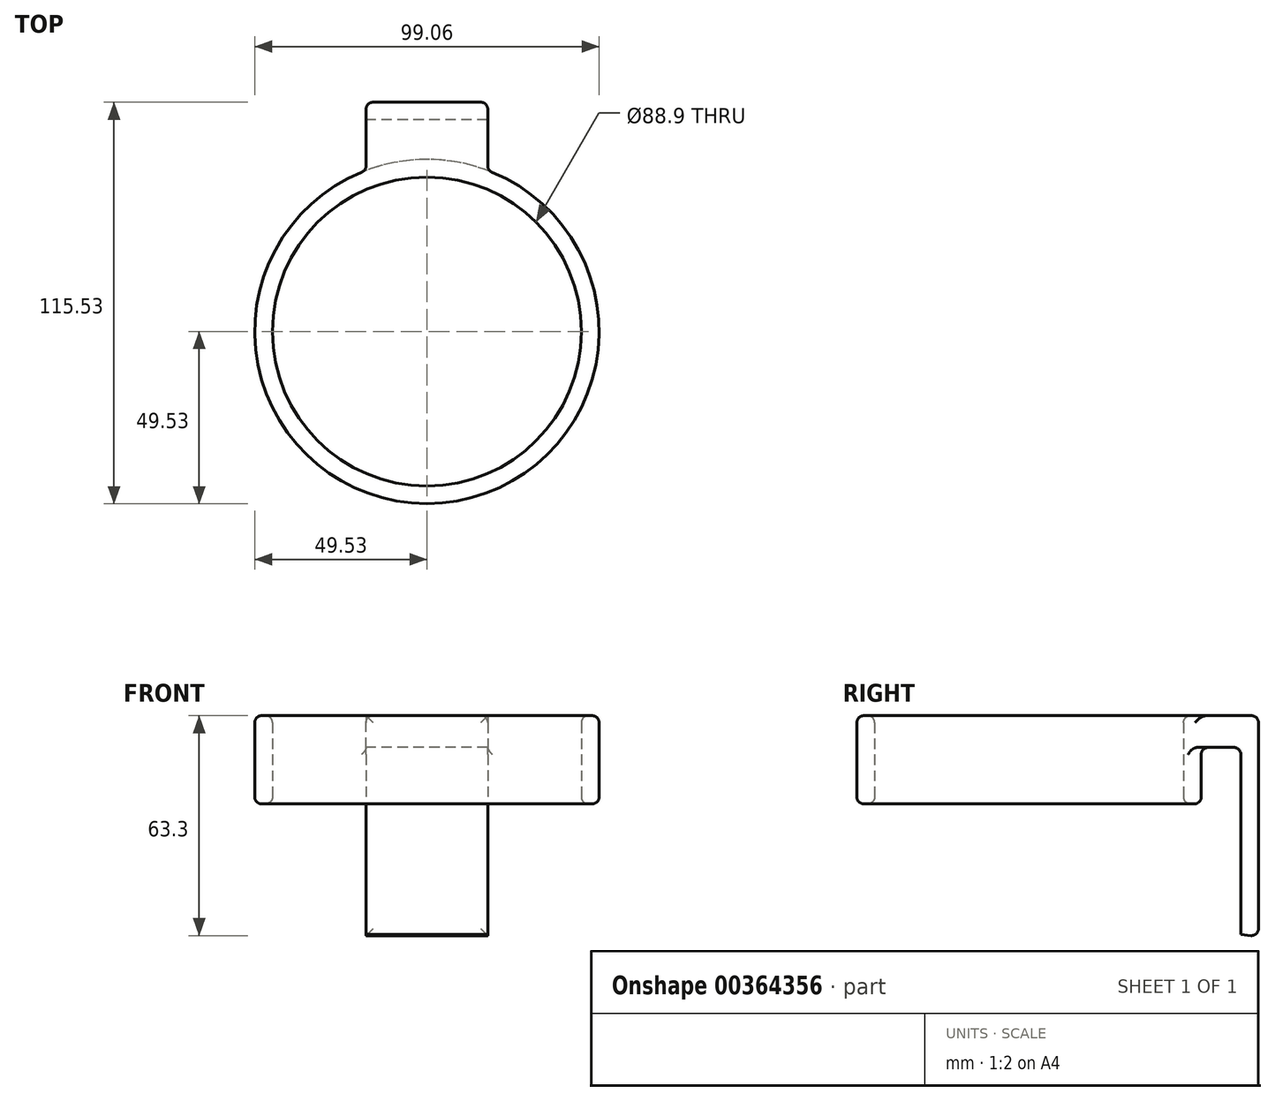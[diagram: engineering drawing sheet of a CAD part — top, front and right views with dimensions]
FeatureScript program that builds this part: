
annotation { "Feature Type Name" : "Feature", "Feature Type Description" : "" }
export const myFeature = defineFeature(function(context is Context, id is Id, definition is map)
    precondition{}
    {
        {
            var Q0;
            Q0=qCreatedBy(makeId("Top.planeOp"),FACE);
            var sketch = newSketch(context, id + "F0", { "sketchPlane" : qUnion([Q0])});
            skCircle(sketch, "E0", {"center": v(0, 0) * mm, "radius": 44.45 * mm});
            skCircle(sketch, "E1", {"center": v(0, 0) * mm, "radius": 49.53 * mm});
            skSolve(sketch);
        }
        {
            var Q0;
            Q0 = qSketchRegion(id + "F0", true);
            extrude(context, id + "F1", {"entities" : qUnion([Q0]), "depth" : 25.4 * mm});
        }
        {
            var Q0;
            Q0=qCreatedBy(makeId("Right.planeOp"),FACE);
            var sketch = newSketch(context, id + "F2", { "sketchPlane" : qUnion([Q0])});
            skLineSegment(sketch, "E2", {"start": v(45.68, 25.4) * mm, "end": v(66, 25.4) * mm});
            skLineSegment(sketch, "E3", {"start": v(66, 25.4) * mm, "end": v(66, 25.4) * mm});
            skLineSegment(sketch, "E4", {"start": v(66, -38.1) * mm, "end": v(66, 25.4) * mm});
            skLineSegment(sketch, "E5", {"start": v(45.68, 25.4) * mm, "end": v(45.68, 16.24) * mm});
            skLineSegment(sketch, "E6", {"start": v(45.68, 16.24) * mm, "end": v(45.68, 16.24) * mm});
            skLineSegment(sketch, "E7", {"start": v(45.68, 16.24) * mm, "end": v(60.96, 16.24) * mm});
            skLineSegment(sketch, "E8", {"start": v(60.96, 16.24) * mm, "end": v(60.96, -37.61) * mm});
            skLineSegment(sketch, "E9", {"start": v(60.96, -37.61) * mm, "end": v(66, -38.1) * mm});
            skPoint(sketch, "E10.start.orphan", {"position": v(60.96, 17.2) * mm});
            skSolve(sketch);
        }
        {
            var Q0;
            Q0 = qSketchRegion(id + "F2", true);
            var Q1;
            Q1=makeQuery(id+"F1.opExtrude","SWEPT_FACE",FACE,{"disambiguationData":[OSD([sQuery(id+"F0.wireOp",EDGE,"E1")])]});
            var Q2;
            Q2=makeQuery(id+"F1.opExtrude","SWEPT_BODY",BODY,{"disambiguationData":[OSD([sQuery(id+"F0.wireOp",EDGE,"E0"),sQuery(id+"F0.wireOp",EDGE,"E1")])]});
            extrude(context, id + "F3", {"entities" : qUnion([Q0]), "operationType" : NewBodyOperationType.ADD, "endBound" : BoundingType.SYMMETRIC, "endBoundEntityFace" : qUnion([Q1]), "endBoundEntityBody" : qUnion([Q2]), "depth" : 35 * mm});
        }
        {
            var Q0;
            Q0=makeQuery(id+"F3.opExtrude","SWEPT_EDGE",EDGE,{"disambiguationData":[OSD([sQuery(id+"F2.wireOp",EDGE,"E7"),sQuery(id+"F2.wireOp",EDGE,"E8")])]});
            var Q1;
            Q1=makeQuery(id+"F3.boolean.opBoolean","INTERSECT",EDGE,{"derivedFrom":[makeQuery(id+"F1.opExtrude","SWEPT_FACE",FACE,{"disambiguationData":[OSD([sQuery(id+"F0.wireOp",EDGE,"E1")])]}),makeQuery(id+"F3.opExtrude","SWEPT_FACE",FACE,{"disambiguationData":[OSD([sQuery(id+"F2.wireOp",EDGE,"E7")])]})]});
            var Q2;
            Q2=makeQuery(id+"F3.boolean.opBoolean","INTERSECT",EDGE,{"derivedFrom":[makeQuery(id+"F1.opExtrude","SWEPT_FACE",FACE,{"disambiguationData":[OSD([sQuery(id+"F0.wireOp",EDGE,"E1")])]}),makeQuery(id+"F3.opExtrude","CAP_FACE",FACE,{"disambiguationData":[OSD([sQuery(id+"F2.wireOp",EDGE,"E2"),sQuery(id+"F2.wireOp",EDGE,"E4"),sQuery(id+"F2.wireOp",EDGE,"E5"),sQuery(id+"F2.wireOp",EDGE,"E7"),sQuery(id+"F2.wireOp",EDGE,"E8"),sQuery(id+"F2.wireOp",EDGE,"E9")])],"isStart":false})]});
            var Q3;
            Q3=makeQuery(id+"F3.boolean.opBoolean","INTERSECT",EDGE,{"derivedFrom":[makeQuery(id+"F1.opExtrude","SWEPT_FACE",FACE,{"disambiguationData":[OSD([sQuery(id+"F0.wireOp",EDGE,"E1")])]}),makeQuery(id+"F3.opExtrude","CAP_FACE",FACE,{"disambiguationData":[OSD([sQuery(id+"F2.wireOp",EDGE,"E2"),sQuery(id+"F2.wireOp",EDGE,"E4"),sQuery(id+"F2.wireOp",EDGE,"E5"),sQuery(id+"F2.wireOp",EDGE,"E7"),sQuery(id+"F2.wireOp",EDGE,"E8"),sQuery(id+"F2.wireOp",EDGE,"E9")])],"isStart":true})]});
            var Q4;
            Q4=makeQuery(id+"F3.opExtrude","SWEPT_EDGE",EDGE,{"disambiguationData":[OSD([sQuery(id+"F2.wireOp",EDGE,"E2"),sQuery(id+"F2.wireOp",EDGE,"E4")])]});
            var Q5;
            Q5=makeQuery(id+"F1.opExtrude","CAP_EDGE",EDGE,{"disambiguationData":[OSD([sQuery(id+"F0.wireOp",EDGE,"E0")])],"isStart":false});
            var Q6;
            Q6=makeQuery(id+"F1.opExtrude","SWEPT_FACE",FACE,{"disambiguationData":[OSD([sQuery(id+"F0.wireOp",EDGE,"E1")])]});
            var Q7;
            Q7=makeQuery(id+"F1.opExtrude","SWEPT_FACE",FACE,{"disambiguationData":[OSD([sQuery(id+"F0.wireOp",EDGE,"E0")])]});
            var Q8;
            Q8=makeQuery(id+"F3.opExtrude","SWEPT_FACE",FACE,{"disambiguationData":[OSD([sQuery(id+"F2.wireOp",EDGE,"E4")])]});
            fillet(context, id + "F4", {"entities" : qUnion([Q0, Q1, Q2, Q3, Q4, Q5, Q6, Q7, Q8]), "radius" : 2 * mm, "tangentPropagation" : true, "allowEdgeOverflow" : false});
        }
    });
